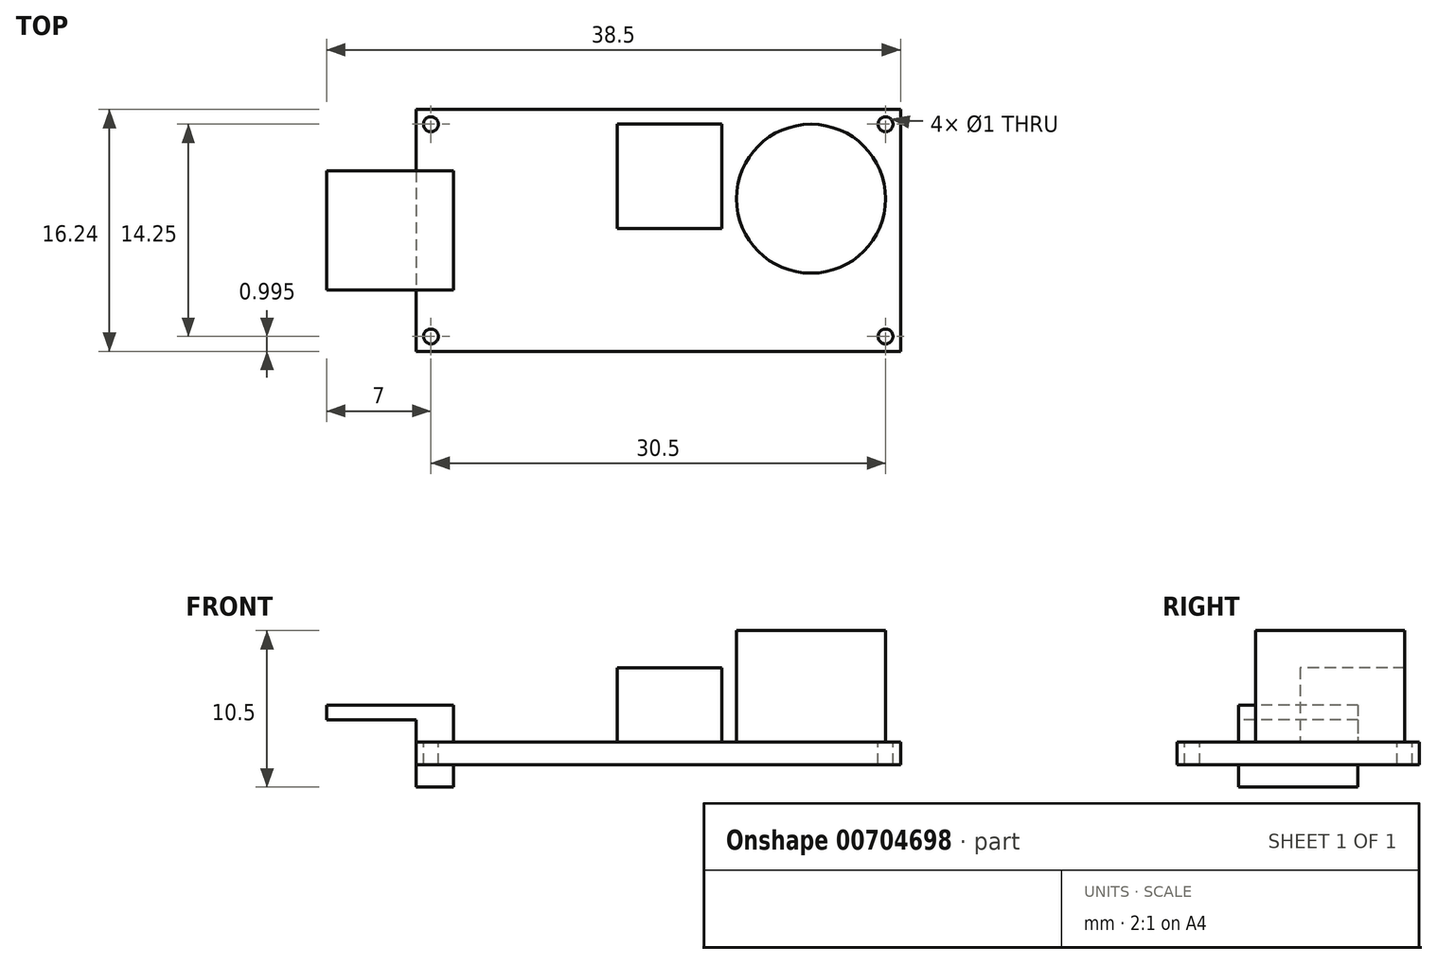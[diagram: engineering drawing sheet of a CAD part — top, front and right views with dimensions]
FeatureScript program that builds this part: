
annotation { "Feature Type Name" : "Feature", "Feature Type Description" : "" }
export const myFeature = defineFeature(function(context is Context, id is Id, definition is map)
    precondition{}
    {
        {
            var Q0;
            Q0=qCreatedBy(makeId("Top.planeOp"),FACE);
            var sketch = newSketch(context, id + "F0", { "sketchPlane" : qUnion([Q0])});
            skLineSegment(sketch, "E0.bottom", {"start": v(-16.25, 8.12) * mm, "end": v(16.25, 8.13) * mm});
            skLineSegment(sketch, "E0.top", {"start": v(-16.25, -8.13) * mm, "end": v(16.25, -8.12) * mm});
            skLineSegment(sketch, "E0.left", {"start": v(-16.25, 8.12) * mm, "end": v(-16.25, -8.13) * mm});
            skLineSegment(sketch, "E0.right", {"start": v(16.25, 8.12) * mm, "end": v(16.25, -8.12) * mm});
            skLineSegment(sketch, "E1.bottom", {"start": v(-2.75, 7.12) * mm, "end": v(4.25, 7.12) * mm});
            skLineSegment(sketch, "E1.top", {"start": v(-2.75, 0.12) * mm, "end": v(4.25, 0.12) * mm});
            skLineSegment(sketch, "E1.left", {"start": v(-2.75, 7.12) * mm, "end": v(-2.75, 0.12) * mm});
            skLineSegment(sketch, "E1.right", {"start": v(4.25, 7.12) * mm, "end": v(4.25, 0.13) * mm});
            skCircle(sketch, "E2", {"center": v(10.25, 2.13) * mm, "radius": 5 * mm});
            skLineSegment(sketch, "E3.bottom", {"start": v(-16.25, 4) * mm, "end": v(-13.75, 4) * mm});
            skLineSegment(sketch, "E3.top", {"start": v(-16.25, -4) * mm, "end": v(-13.75, -4) * mm});
            skLineSegment(sketch, "E3.left", {"start": v(-16.25, 4) * mm, "end": v(-16.25, -4) * mm});
            skLineSegment(sketch, "E3.right", {"start": v(-13.75, 4) * mm, "end": v(-13.75, -4) * mm});
            skLineSegment(sketch, "E4.bottom", {"start": v(-16.25, 4) * mm, "end": v(-22.25, 4) * mm});
            skLineSegment(sketch, "E4.top", {"start": v(-16.25, -4) * mm, "end": v(-22.25, -4) * mm});
            skLineSegment(sketch, "E4.right", {"start": v(-22.25, 4) * mm, "end": v(-22.25, -4) * mm});
            skCircle(sketch, "E5", {"center": v(15.25, 7.13) * mm, "radius": 0.5 * mm});
            skCircle(sketch, "E6", {"center": v(15.25, -7.12) * mm, "radius": 0.5 * mm});
            skCircle(sketch, "E7", {"center": v(-15.25, 7.12) * mm, "radius": 0.5 * mm});
            skCircle(sketch, "E8", {"center": v(-15.25, -7.13) * mm, "radius": 0.5 * mm});
            skSolve(sketch);
        }
        {
            var Q0;
            {var subQ0=sQuery(id+"F0.wireOp",EDGE,"E0.bottom");Q0=makeQuery(id+"F0.imprint","IMPRINT",FACE,{"disambiguationData":[TD([[makeQuery(id+"F0.imprint","IMPRINT",EDGE,{"derivedFrom":subQ0}),-1.0]])]});}
            var Q1;
            {var subQ0=sQuery(id+"F0.wireOp",EDGE,"E3.bottom");Q1=makeQuery(id+"F0.imprint","IMPRINT",FACE,{"disambiguationData":[TD([[makeQuery(id+"F0.imprint","IMPRINT",EDGE,{"derivedFrom":subQ0}),-1.0]])]});}
            var Q2;
            Q2=makeQuery(id+"F0.imprint","IMPRINT",FACE,{"disambiguationData":[TD([[makeQuery(id+"F0.imprint","IMPRINT",EDGE,{"derivedFrom":sQuery(id+"F0.wireOp",EDGE,"E1.bottom")}),-1.0]])]});
            var Q3;
            Q3=makeQuery(id+"F0.imprint","IMPRINT",FACE,{"disambiguationData":[TD([[makeQuery(id+"F0.imprint","IMPRINT",EDGE,{"derivedFrom":sQuery(id+"F0.wireOp",EDGE,"E2")}),1.0]])]});
            extrude(context, id + "F1", {"entities" : qUnion([Q0, Q1, Q2, Q3]), "oppositeDirection" : true, "depth" : 1.5 * mm, "offsetDistance" : 25 * mm});
        }
        {
            var Q0;
            Q0=makeQuery(id+"F0.imprint","IMPRINT",FACE,{"disambiguationData":[TD([[makeQuery(id+"F0.imprint","IMPRINT",EDGE,{"derivedFrom":sQuery(id+"F0.wireOp",EDGE,"E2")}),1.0]])]});
            extrude(context, id + "F2", {"entities" : qUnion([Q0]), "operationType" : NewBodyOperationType.ADD, "depth" : 7.5 * mm, "offsetDistance" : 25 * mm});
        }
        {
            var Q0;
            Q0=makeQuery(id+"F0.imprint","IMPRINT",FACE,{"disambiguationData":[TD([[makeQuery(id+"F0.imprint","IMPRINT",EDGE,{"derivedFrom":sQuery(id+"F0.wireOp",EDGE,"E1.bottom")}),-1.0]])]});
            extrude(context, id + "F3", {"entities" : qUnion([Q0]), "operationType" : NewBodyOperationType.ADD, "depth" : 5 * mm, "offsetDistance" : 25 * mm});
        }
        {
            var Q0;
            {var subQ0=sQuery(id+"F0.wireOp",EDGE,"E3.bottom");Q0=makeQuery(id+"F0.imprint","IMPRINT",FACE,{"disambiguationData":[TD([[makeQuery(id+"F0.imprint","IMPRINT",EDGE,{"derivedFrom":subQ0}),-1.0]])]});}
            extrude(context, id + "F4", {"entities" : qUnion([Q0]), "operationType" : NewBodyOperationType.ADD, "depth" : 2.5 * mm, "offsetDistance" : 25 * mm, "hasSecondDirection" : true, "secondDirectionOppositeDirection" : true, "secondDirectionDepth" : 3 * mm});
        }
        {
            var Q0;
            {var subQ0=sQuery(id+"F0.wireOp",EDGE,"E4.bottom");Q0=makeQuery(id+"F0.imprint","IMPRINT",FACE,{"disambiguationData":[TD([[makeQuery(id+"F0.imprint","IMPRINT",EDGE,{"derivedFrom":subQ0}),1.0]])]});}
            extrude(context, id + "F5", {"entities" : qUnion([Q0]), "operationType" : NewBodyOperationType.ADD, "depth" : 2.5 * mm, "offsetDistance" : 25 * mm, "hasSecondDirection" : true, "secondDirectionOppositeDirection" : false, "secondDirectionDepth" : 1.5 * mm});
        }
    });
